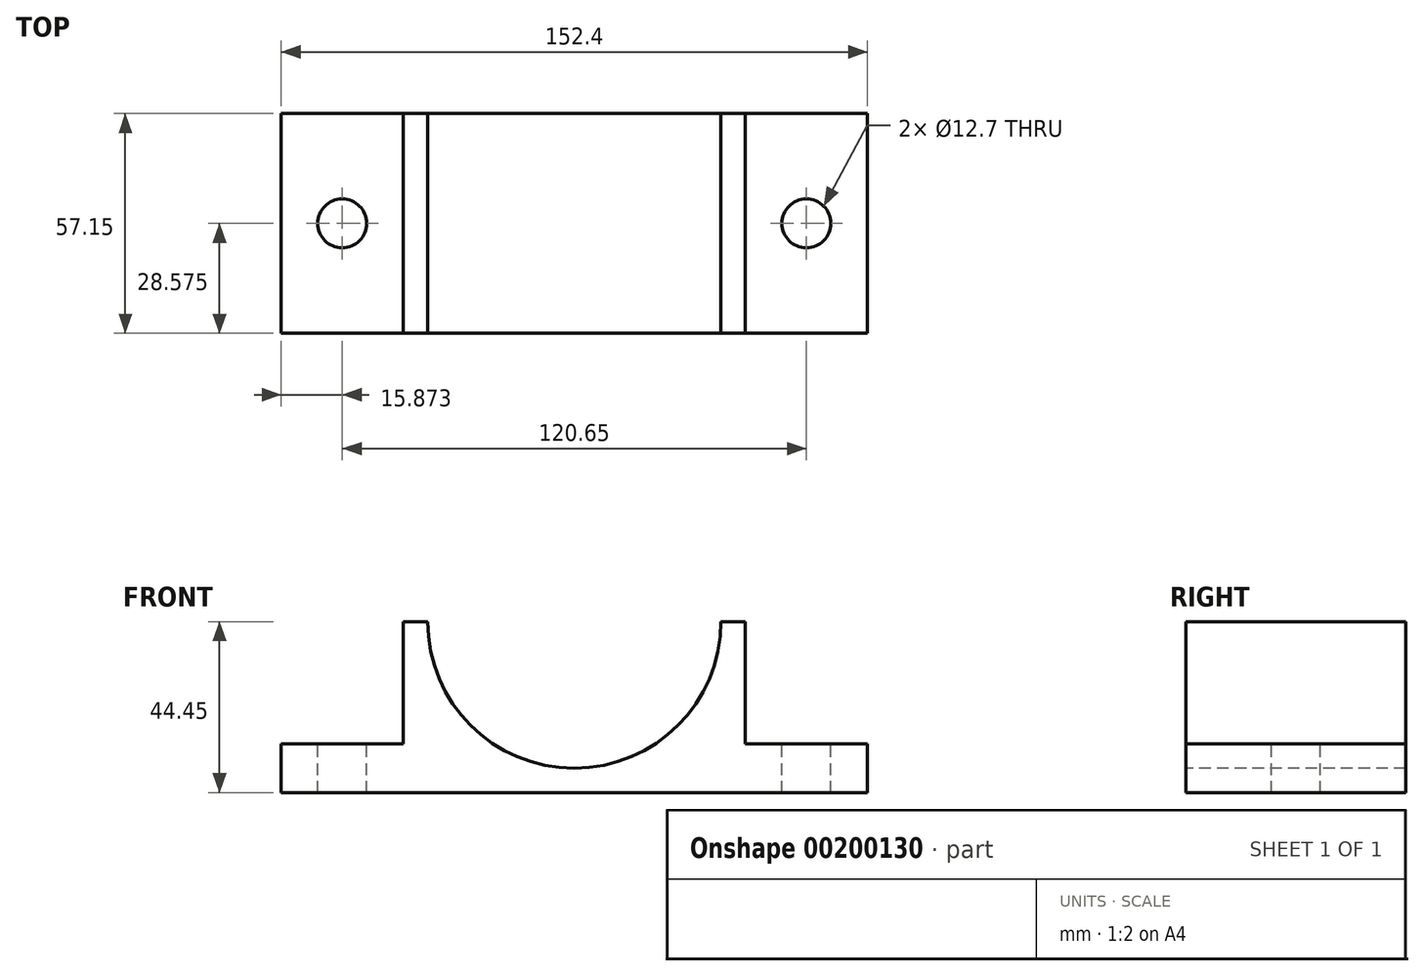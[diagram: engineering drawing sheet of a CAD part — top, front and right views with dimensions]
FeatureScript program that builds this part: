
annotation { "Feature Type Name" : "Feature", "Feature Type Description" : "" }
export const myFeature = defineFeature(function(context is Context, id is Id, definition is map)
    precondition{}
    {
        {
            var Q0;
            Q0=qCreatedBy(makeId("Front.planeOp"),FACE);
            var sketch = newSketch(context, id + "F0", { "sketchPlane" : qUnion([Q0])});
            skLineSegment(sketch, "E0.bottom", {"start": v(-69.6, -16.47) * mm, "end": v(-37.85, -16.47) * mm});
            skLineSegment(sketch, "E0.top", {"start": v(-69.6, -29.17) * mm, "end": v(82.8, -29.17) * mm});
            skLineSegment(sketch, "E0.left", {"start": v(-69.6, -16.47) * mm, "end": v(-69.6, -29.17) * mm});
            skLineSegment(sketch, "E0.right", {"start": v(82.8, -16.47) * mm, "end": v(82.8, -29.17) * mm});
            skLineSegment(sketch, "E1.top", {"start": v(-37.85, 15.28) * mm, "end": v(-31.5, 15.28) * mm});
            skLineSegment(sketch, "E1.left", {"start": v(-37.85, -16.47) * mm, "end": v(-37.85, 15.28) * mm});
            skLineSegment(sketch, "E1.right", {"start": v(51.05, -16.47) * mm, "end": v(51.05, 15.28) * mm});
            skArc(sketch, "E2", {"start": v(-31.5, 15.28) * mm, "mid": v(6.6, -22.82) * mm, "end": v(44.7, 15.28) * mm});
            skLineSegment(sketch, "E3.trimOffspring", {"start": v(44.7, 15.28) * mm, "end": v(51.05, 15.28) * mm});
            skLineSegment(sketch, "E4.trimOffspring", {"start": v(51.05, -16.47) * mm, "end": v(82.8, -16.47) * mm});
            skSolve(sketch);
        }
        {
            var Q0;
            Q0=makeQuery(id+"F0.imprint","IMPRINT",FACE,{"disambiguationData":[TD([[makeQuery(id+"F0.imprint","IMPRINT",EDGE,{"derivedFrom":sQuery(id+"F0.wireOp",EDGE,"E0.bottom")}),-1.0]])]});
            extrude(context, id + "F1", {"entities" : qUnion([Q0]), "oppositeDirection" : true, "depth" : 57.15 * mm});
        }
        {
            var Q0;
            Q0=makeQuery(id+"F1.opExtrude","SWEPT_FACE",FACE,{"disambiguationData":[OSD([sQuery(id+"F0.wireOp",EDGE,"E0.bottom")])]});
            var sketch = newSketch(context, id + "F2", { "sketchPlane" : qUnion([Q0])});
            skCircle(sketch, "E5", {"center": v(66.92, 28.58) * mm, "radius": 6.35 * mm});
            skCircle(sketch, "E6", {"center": v(-53.73, 28.58) * mm, "radius": 6.35 * mm});
            skSolve(sketch);
        }
        {
            var Q0;
            Q0=makeQuery(id+"F2.imprint","IMPRINT",FACE,{"disambiguationData":[TD([[makeQuery(id+"F2.imprint","IMPRINT",EDGE,{"derivedFrom":sQuery(id+"F2.wireOp",EDGE,"E6")}),1.0]])]});
            var Q1;
            Q1=makeQuery(id+"F2.imprint","IMPRINT",FACE,{"disambiguationData":[TD([[makeQuery(id+"F2.imprint","IMPRINT",EDGE,{"derivedFrom":sQuery(id+"F2.wireOp",EDGE,"E5")}),1.0]])]});
            extrude(context, id + "F3", {"entities" : qUnion([Q0, Q1]), "operationType" : NewBodyOperationType.REMOVE, "oppositeDirection" : true, "depth" : 53.85 * mm});
        }
    });
